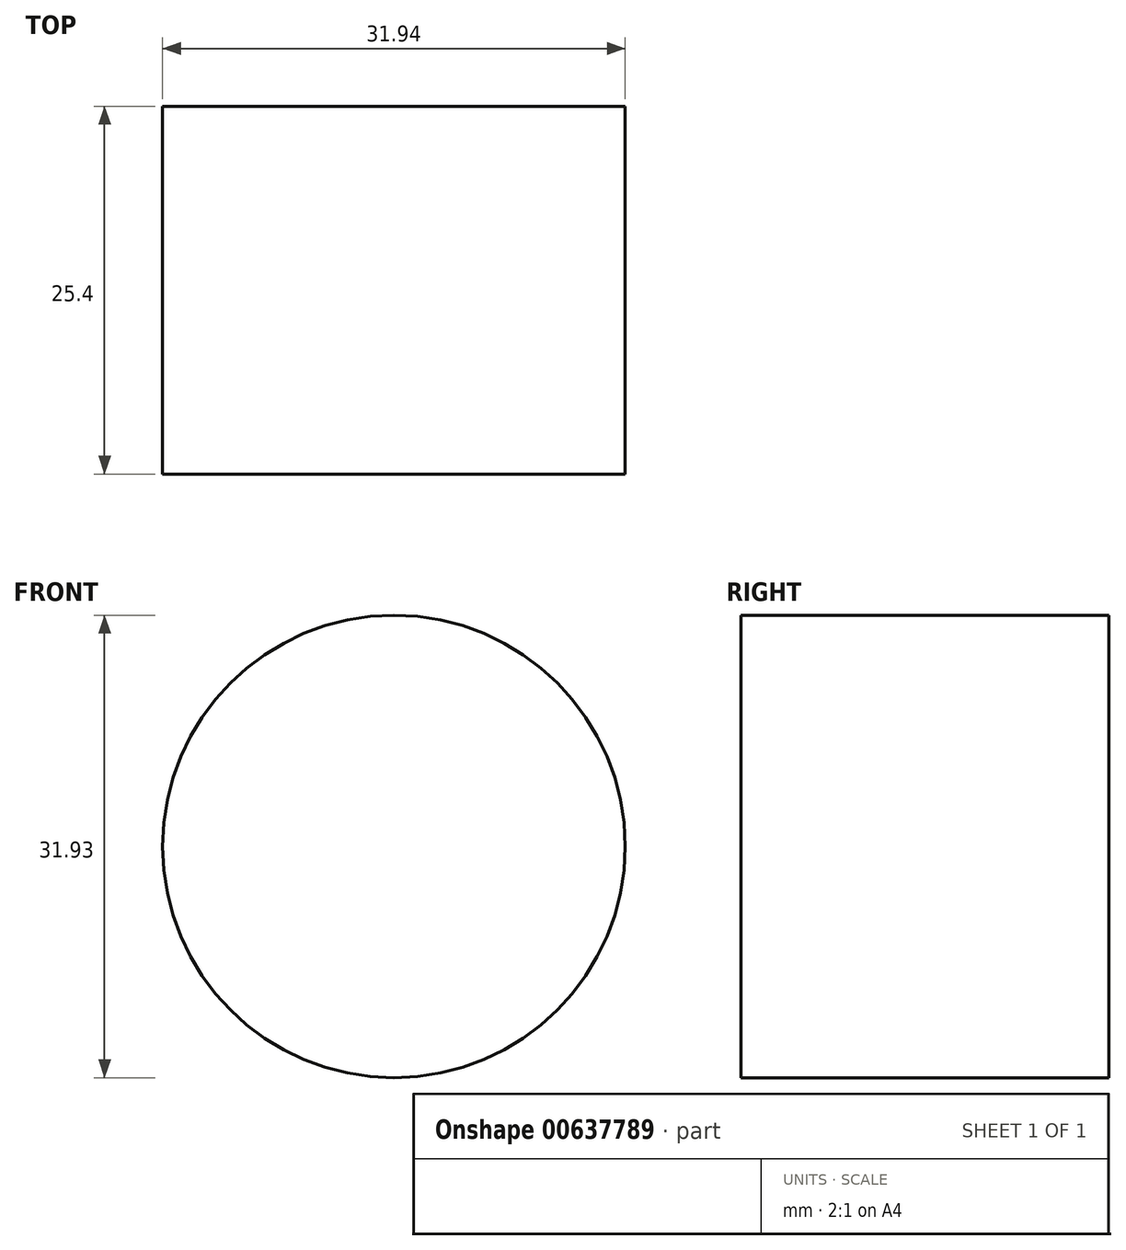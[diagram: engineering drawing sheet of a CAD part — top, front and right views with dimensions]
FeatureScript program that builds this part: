
annotation { "Feature Type Name" : "Feature", "Feature Type Description" : "" }
export const myFeature = defineFeature(function(context is Context, id is Id, definition is map)
    precondition{}
    {
        {
            var Q0;
            Q0=qCreatedBy(makeId("Front.planeOp"),FACE);
            var sketch = newSketch(context, id + "F0", { "sketchPlane" : qUnion([Q0])});
            skCircle(sketch, "E0", {"center": v(0, -2.73) * mm, "radius": 15.97 * mm});
            skSolve(sketch);
        }
        {
            var Q0;
            Q0=makeQuery(id+"F0.imprint","IMPRINT",FACE,{"disambiguationData":[TD([[makeQuery(id+"F0.imprint","IMPRINT",EDGE,{"derivedFrom":sQuery(id+"F0.wireOp",EDGE,"E0")}),1.0]])]});
            extrude(context, id + "F1", {"entities" : qUnion([Q0]), "depth" : 25.4 * mm, "offsetDistance" : 25.4 * mm});
        }
    });
